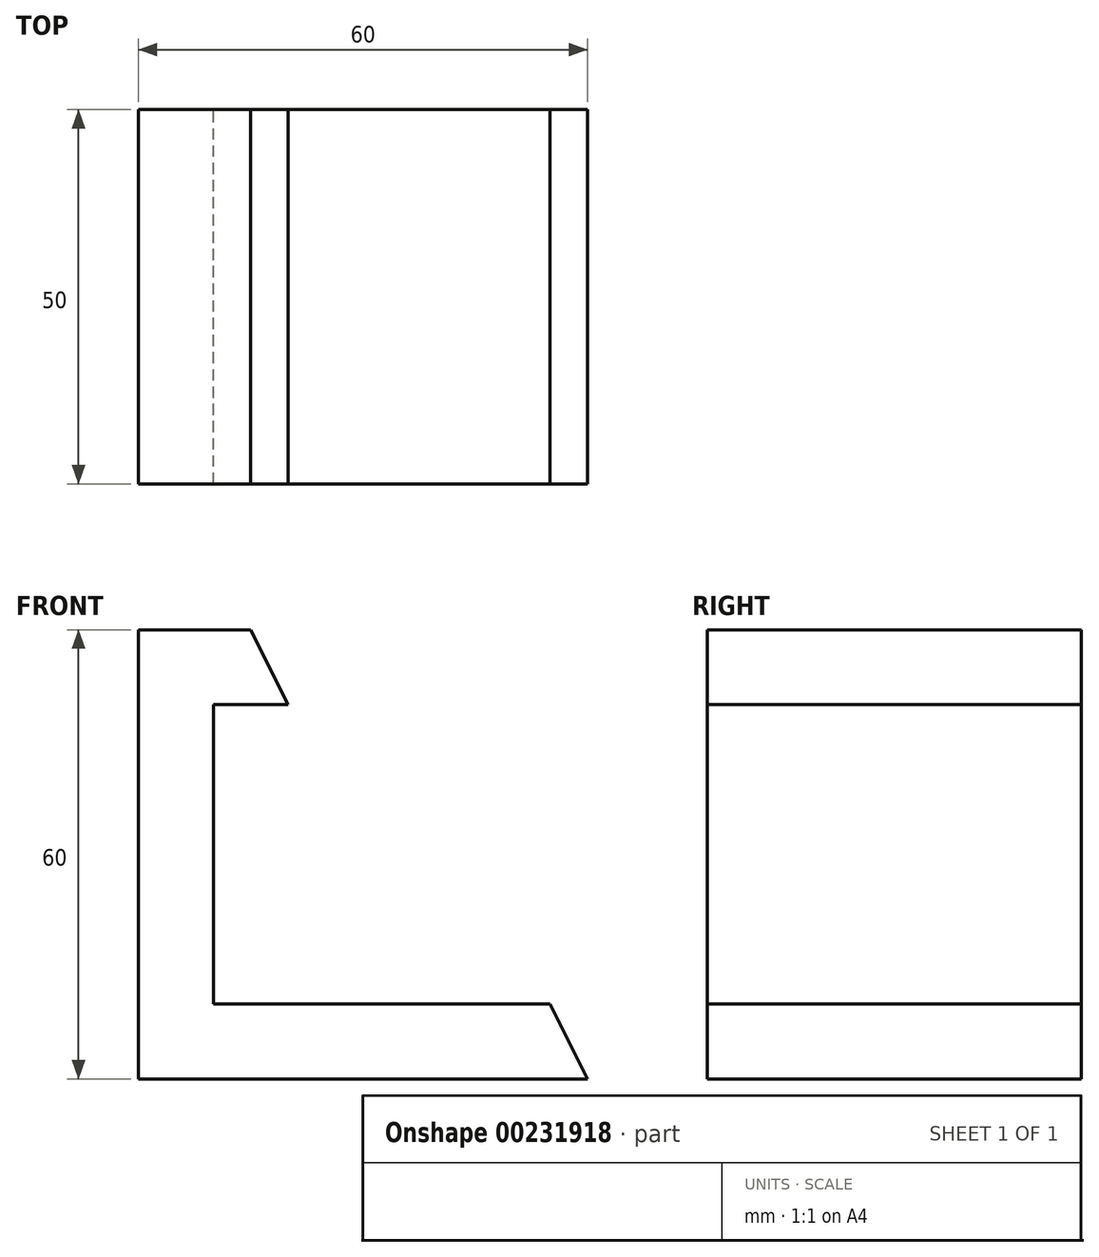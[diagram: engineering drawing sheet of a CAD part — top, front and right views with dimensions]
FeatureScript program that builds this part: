
annotation { "Feature Type Name" : "Feature", "Feature Type Description" : "" }
export const myFeature = defineFeature(function(context is Context, id is Id, definition is map)
    precondition{}
    {
        {
            var Q0;
            Q0=qCreatedBy(makeId("Front.planeOp"),FACE);
            var sketch = newSketch(context, id + "F0", { "sketchPlane" : qUnion([Q0])});
            skLineSegment(sketch, "E0", {"start": v(0, 0) * mm, "end": v(-60, 0) * mm});
            skLineSegment(sketch, "E1", {"start": v(-60, 0) * mm, "end": v(-60, 60) * mm});
            skLineSegment(sketch, "E2", {"start": v(-60, 60) * mm, "end": v(-45, 60) * mm});
            skLineSegment(sketch, "E3", {"start": v(-45, 60) * mm, "end": v(-40, 50) * mm});
            skLineSegment(sketch, "E4", {"start": v(-40, 50) * mm, "end": v(-50, 50) * mm});
            skLineSegment(sketch, "E5", {"start": v(-50, 50) * mm, "end": v(-50, 10) * mm});
            skLineSegment(sketch, "E6", {"start": v(-50, 10) * mm, "end": v(-5, 10) * mm});
            skLineSegment(sketch, "E7", {"start": v(-5, 10) * mm, "end": v(0, 0) * mm});
            skSolve(sketch);
        }
        {
            var Q0;
            Q0=makeQuery(id+"F0.imprint","IMPRINT",FACE,{"disambiguationData":[TD([[makeQuery(id+"F0.imprint","IMPRINT",EDGE,{"derivedFrom":sQuery(id+"F0.wireOp",EDGE,"E0")}),-1.0]])]});
            extrude(context, id + "F1", {"entities" : qUnion([Q0]), "depth" : 50 * mm});
        }
    });
